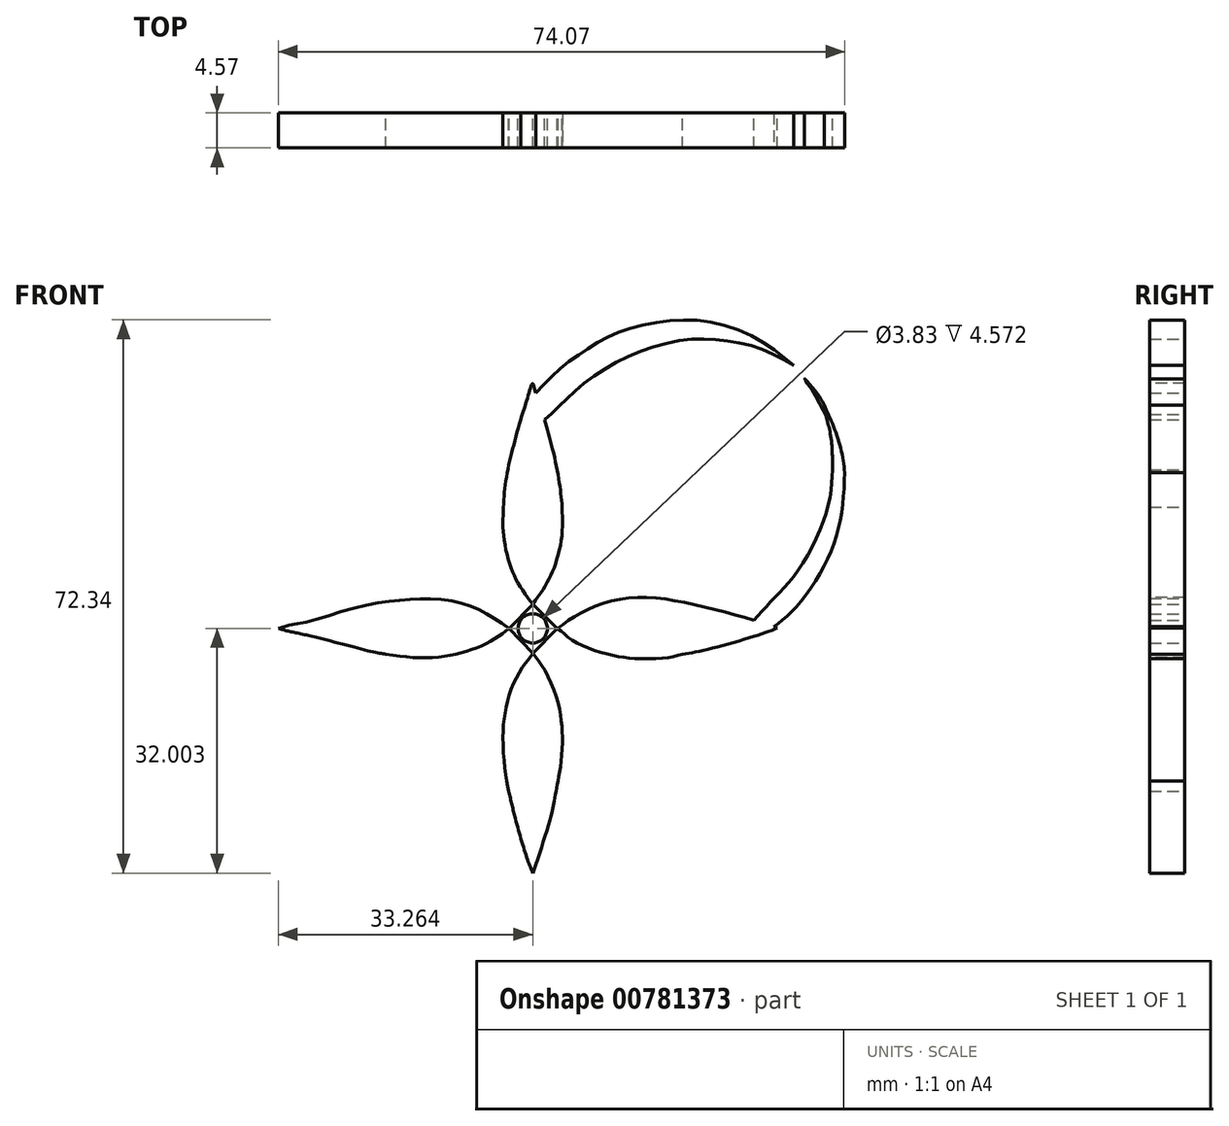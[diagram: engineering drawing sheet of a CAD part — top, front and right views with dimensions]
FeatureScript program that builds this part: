
annotation { "Feature Type Name" : "Feature", "Feature Type Description" : "" }
export const myFeature = defineFeature(function(context is Context, id is Id, definition is map)
    precondition{}
    {
        {
            var Q0;
            Q0=qCreatedBy(makeId("Front.planeOp"),FACE);
            var sketch = newSketch(context, id + "F0", { "sketchPlane" : qUnion([Q0])});
            skFitSpline(sketch, "E0", {"points": [v(1.14, 20.31) * mm, v(-0.69, 22.96) * mm, v(-1.96, 25.91) * mm, v(-2.7, 29.66) * mm, v(-2.7, 32.48) * mm], "startDerivative": vector(-7.54, 10.16) * mm, "endDerivative": vector(0.56, 11.5) * mm});
            skLineSegment(sketch, "E1", {"start": v(-1.93, 17.17) * mm, "end": v(1.14, 20.31) * mm});
            skLineSegment(sketch, "E2", {"start": v(1.14, 20.31) * mm, "end": v(4.35, 17.17) * mm});
            skLineSegment(sketch, "E3", {"start": v(4.35, 17.17) * mm, "end": v(1.14, 13.9) * mm});
            skLineSegment(sketch, "E4", {"start": v(1.14, 13.9) * mm, "end": v(-1.93, 17.17) * mm});
            skFitSpline(sketch, "E5", {"points": [v(1.14, 20.31) * mm, v(2.92, 22.96) * mm, v(4.1, 25.58) * mm, v(4.94, 29.2) * mm, v(4.99, 33.04) * mm], "startDerivative": vector(8.06, 11.56) * mm, "endDerivative": vector(-0.56, 14.55) * mm});
            skFitSpline(sketch, "E6", {"points": [v(4.35, 17.17) * mm, v(6.86, 18.87) * mm, v(10.57, 20.52) * mm, v(15.35, 21.25) * mm, v(20.98, 20.56) * mm, v(27.55, 18.97) * mm, v(33.14, 17.22) * mm], "startDerivative": vector(19.47, 13.29) * mm, "endDerivative": vector(30.07, -9.77) * mm});
            skFitSpline(sketch, "E7", {"points": [v(-2.7, 32.48) * mm, v(-2.43, 36.1) * mm, v(-1.62, 40.04) * mm, v(-0.45, 44.44) * mm], "startDerivative": vector(0.52, 11.44) * mm, "endDerivative": vector(3.45, 12.62) * mm});
            skFitSpline(sketch, "E8", {"points": [v(4.99, 33.04) * mm, v(4.63, 36.22) * mm, v(3.68, 40.87) * mm, v(2.67, 44.47) * mm], "startDerivative": vector(-0.89, 9.86) * mm, "endDerivative": vector(-3.1, 10.43) * mm});
            skFitSpline(sketch, "E9", {"points": [v(-0.45, 44.44) * mm, v(0.64, 47.93) * mm, v(1.14, 49.22) * mm, v(1.4, 48.38) * mm, v(1.96, 46.96) * mm, v(2.67, 44.47) * mm], "startDerivative": vector(4.34, 12.87) * mm, "endDerivative": vector(3.09, -10.34) * mm});
            skFitSpline(sketch, "E10", {"points": [v(4.35, 17.17) * mm, v(5.84, 15.98) * mm, v(8.4, 14.6) * mm, v(11.88, 13.6) * mm, v(14.66, 13.23) * mm, v(18.64, 13.34) * mm, v(20.7, 13.76) * mm], "startDerivative": vector(11.64, -7.76) * mm, "endDerivative": vector(12.88, 2.46) * mm});
            skFitSpline(sketch, "E11", {"points": [v(20.7, 13.76) * mm, v(23.97, 14.43) * mm, v(30.33, 16.2) * mm, v(33.14, 17.22) * mm], "startDerivative": vector(9.66, 1.72) * mm, "endDerivative": vector(8.54, 3.31) * mm});
            skFitSpline(sketch, "E12", {"points": [v(-1.93, 17.17) * mm, v(-4.7, 18.98) * mm, v(-7.75, 20.34) * mm, v(-12.2, 21.05) * mm, v(-16.66, 20.81) * mm, v(-22.25, 19.83) * mm, v(-28.49, 18) * mm, v(-32.12, 17.17) * mm], "startDerivative": vector(-23.19, 14.81) * mm, "endDerivative": vector(-38, -14.07) * mm});
            skFitSpline(sketch, "E13", {"points": [v(-1.93, 17.17) * mm, v(-4.2, 15.57) * mm, v(-7.57, 14.17) * mm, v(-12.03, 13.34) * mm, v(-18.04, 13.8) * mm], "startDerivative": vector(-10.63, -7.82) * mm, "endDerivative": vector(-20.77, 3.43) * mm});
            skFitSpline(sketch, "E14", {"points": [v(-32.12, 17.17) * mm, v(-27.43, 16.07) * mm, v(-19.98, 14.14) * mm, v(-18.04, 13.8) * mm], "startDerivative": vector(9, -3.07) * mm, "endDerivative": vector(6.58, -0.88) * mm});
            skFitSpline(sketch, "E15", {"points": [v(1.14, 13.9) * mm, v(2.45, 12.14) * mm, v(4.21, 8.32) * mm, v(4.88, 5.04) * mm, v(5.04, 2.39) * mm, v(4.78, -0.8) * mm, v(4.44, -2.79) * mm], "startDerivative": vector(9.16, -10.98) * mm, "endDerivative": vector(-2.45, -13.3) * mm});
            skFitSpline(sketch, "E16", {"points": [v(4.44, -2.79) * mm, v(3.9, -5.62) * mm, v(3.52, -7.46) * mm, v(1.17, -14.83) * mm], "startDerivative": vector(-1.54, -9.2) * mm, "endDerivative": vector(-3.82, -11.04) * mm});
            skFitSpline(sketch, "E17", {"points": [v(1.14, 13.9) * mm, v(-0.46, 11.67) * mm, v(-1.76, 8.99) * mm, v(-2.49, 6.07) * mm, v(-2.75, 3.05) * mm, v(-2.45, -1.53) * mm, v(-2, -4.15) * mm], "startDerivative": vector(-10.04, -14.48) * mm, "endDerivative": vector(3.22, -15.47) * mm});
            skFitSpline(sketch, "E18", {"points": [v(-2, -4.15) * mm, v(-0.93, -8.43) * mm, v(0.43, -12.97) * mm, v(1.17, -14.83) * mm], "startDerivative": vector(2.65, -11.17) * mm, "endDerivative": vector(2.82, -6.51) * mm});
            skCircle(sketch, "E19", {"center": v(1.14, 17.17) * mm, "radius": 1.91 * mm});
            skFitSpline(sketch, "E20", {"points": [v(1.57, 47.93) * mm, v(4.7, 51.1) * mm, v(8.33, 53.74) * mm, v(12.32, 55.89) * mm, v(18, 57.28) * mm, v(24.34, 57.23) * mm, v(30.77, 54.85) * mm, v(35.26, 51.55) * mm], "startDerivative": vector(23.36, 25.32) * mm, "endDerivative": vector(28.74, -23.92) * mm});
            skFitSpline(sketch, "E21", {"points": [v(2.67, 44.47) * mm, v(5.34, 46.96) * mm, v(9.13, 50.16) * mm, v(14.52, 53.1) * mm, v(20.65, 54.85) * mm, v(25.89, 54.85) * mm, v(30.77, 53.8) * mm, v(35.26, 51.55) * mm], "startDerivative": vector(23.03, 17.43) * mm, "endDerivative": vector(31.15, -17.83) * mm});
            skFitSpline(sketch, "E22", {"points": [v(30.06, 18.21) * mm, v(32.72, 21.13) * mm, v(36.11, 25.17) * mm, v(39.66, 32.75) * mm, v(40.35, 37.94) * mm], "startDerivative": vector(12.37, 13.95) * mm, "endDerivative": vector(1, 20.14) * mm});
            skFitSpline(sketch, "E23", {"points": [v(32.64, 17.38) * mm, v(35.27, 19.64) * mm, v(39.06, 24.97) * mm, v(41.35, 31.26) * mm, v(41.95, 37.54) * mm], "startDerivative": vector(13.04, 9.86) * mm, "endDerivative": vector(1.05, 23.93) * mm});
            skFitSpline(sketch, "E24", {"points": [v(40.35, 37.94) * mm, v(40.14, 42.09) * mm, v(39.43, 45.17) * mm], "startDerivative": vector(-0.1, 8.08) * mm, "endDerivative": vector(-1.8, 6.35) * mm});
            skFitSpline(sketch, "E25", {"points": [v(41.95, 37.54) * mm, v(41.44, 40.62) * mm, v(40.35, 43.87) * mm, v(39.24, 46.37) * mm], "startDerivative": vector(-1.14, 9.08) * mm, "endDerivative": vector(-3.57, 7.62) * mm});
            skFitSpline(sketch, "E26", {"points": [v(39.43, 45.17) * mm, v(37.44, 48.67) * mm, v(36.7, 49.82) * mm, v(38.44, 47.78) * mm, v(39.24, 46.37) * mm], "startDerivative": vector(-5.89, 11.14) * mm, "endDerivative": vector(2.45, -5.63) * mm});
            skFitSpline(sketch, "E27", {"points": [v(-1.12, -7.69) * mm, v(-4.3, -11.88) * mm, v(-9.73, -16.68) * mm, v(-15.66, -19.57) * mm, v(-21.86, -20.98) * mm, v(-26.45, -20.77) * mm, v(-31.17, -19.15) * mm, v(-33.85, -17.17) * mm, v(-31.08, -20.7) * mm, v(-24.97, -22.89) * mm, v(-18.12, -24.01) * mm, v(-9.24, -21.97) * mm, v(-3.31, -18.3) * mm, v(0.94, -14.29) * mm], "startDerivative": vector(-39.93, -57.02) * mm, "endDerivative": vector(53.19, 53.88) * mm});
            skFitSpline(sketch, "E28", {"points": [v(-31.08, 16.82) * mm, v(-35.18, 13.62) * mm, v(-38.33, 9.5) * mm, v(-40.53, 4.23) * mm, v(-41.76, -2.61) * mm, v(-40.62, -8.76) * mm, v(-38.07, -14.55) * mm, v(-36.23, -16.74) * mm, v(-38.6, -12.44) * mm, v(-39.74, -6.04) * mm, v(-38.77, 1.33) * mm, v(-34.82, 9.5) * mm, v(-29.03, 15.37) * mm, v(-27.43, 16.07) * mm], "startDerivative": vector(-58.16, -40.8) * mm, "endDerivative": vector(32.53, 9.22) * mm});
            skSolve(sketch);
        }
        {
            var Q0;
            Q0 = qSketchRegion(id + "F0", true);
            extrude(context, id + "F1", {"entities" : qUnion([Q0]), "depth" : 4.57 * mm, "offsetDistance" : 25.4 * mm});
        }
    });
